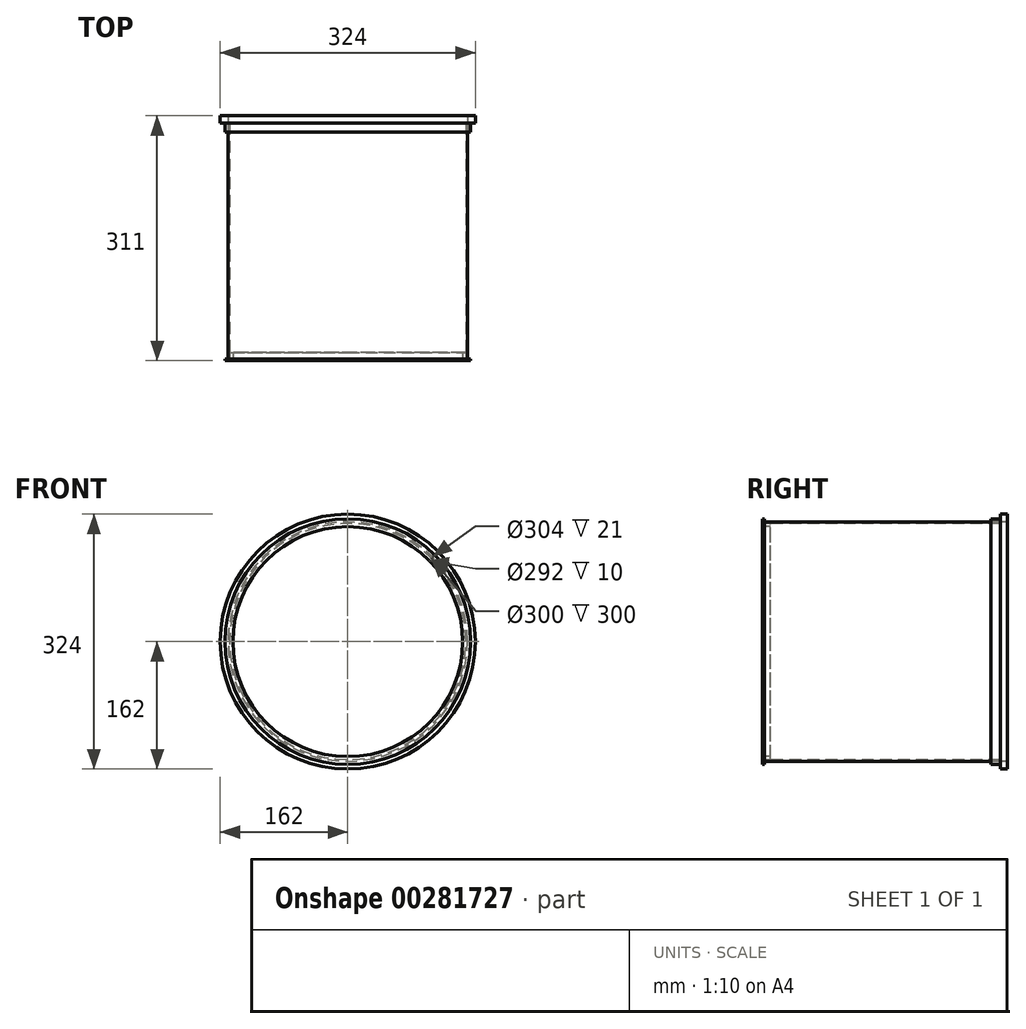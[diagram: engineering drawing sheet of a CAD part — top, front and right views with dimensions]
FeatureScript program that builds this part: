
annotation { "Feature Type Name" : "Feature", "Feature Type Description" : "" }
export const myFeature = defineFeature(function(context is Context, id is Id, definition is map)
    precondition{}
    {
        {
            assignVariable(context, id + "F0", {"name" : "DS_Length", "anyValue" : 300});
        }
        {
            var Q0;
            Q0=qCreatedBy(makeId("Front.planeOp"),FACE);
            var sketch = newSketch(context, id + "F1", { "sketchPlane" : qUnion([Q0])});
            skCircle(sketch, "E0", {"center": v(0, 0) * mm, "radius": 150 * mm});
            skCircle(sketch, "E1", {"center": v(0, 0) * mm, "radius": 152 * mm});
            skSolve(sketch);
        }
        {
            var Q0;
            Q0=makeQuery(id+"F1.imprint","IMPRINT",FACE,{"disambiguationData":[TD([[makeQuery(id+"F1.imprint","IMPRINT",EDGE,{"derivedFrom":sQuery(id+"F1.wireOp",EDGE,"E0")}),-1.0]])]});
            extrude(context, id + "F2", {"entities" : qUnion([Q0]), "oppositeDirection" : true, "depth" : (getVariable(context, 'DS_Length')) * mm, "offsetDistance" : 25 * mm});
        }
        {
            var Q0;
            Q0=qCreatedBy(makeId("Right.planeOp"),FACE);
            var sketch = newSketch(context, id + "F3", { "sketchPlane" : qUnion([Q0])});
            skLineSegment(sketch, "E2", {"start": v(309, 162) * mm, "end": v(309, 152) * mm});
            skLineSegment(sketch, "E3", {"start": v(309, 152) * mm, "end": v(288, 152) * mm});
            skLineSegment(sketch, "E4", {"start": v(288, 152) * mm, "end": v(288, 156) * mm});
            skLineSegment(sketch, "E5", {"start": v(288, 156) * mm, "end": v(300, 156) * mm});
            skLineSegment(sketch, "E6", {"start": v(300, 156) * mm, "end": v(300, 162) * mm});
            skLineSegment(sketch, "E7", {"start": v(300, 162) * mm, "end": v(309, 162) * mm});
            skLineSegment(sketch, "E8", {"start": v(-26.86, 0) * mm, "end": v(353.55, 0) * mm, "construction": true});
            skLineSegment(sketch, "E9", {"start": v(8, 150) * mm, "end": v(8, 146) * mm});
            skLineSegment(sketch, "E10", {"start": v(8, 146) * mm, "end": v(-2, 146) * mm});
            skLineSegment(sketch, "E11", {"start": v(-2, 146) * mm, "end": v(-2, 156) * mm});
            skLineSegment(sketch, "E12", {"start": v(-2, 156) * mm, "end": v(0, 156) * mm});
            skLineSegment(sketch, "E13", {"start": v(0, 156) * mm, "end": v(0, 150) * mm});
            skLineSegment(sketch, "E14", {"start": v(0, 150) * mm, "end": v(8, 150) * mm});
            skSolve(sketch);
        }
        {
            var Q0;
            Q0=makeQuery(id+"F3.imprint","IMPRINT",FACE,{"disambiguationData":[TD([[makeQuery(id+"F3.imprint","IMPRINT",EDGE,{"derivedFrom":sQuery(id+"F3.wireOp",EDGE,"E2")}),-1.0]])]});
            var Q1;
            Q1=sQuery(id+"F3.wireOp",EDGE,"E8");
            revolve(context, id + "F4", {"entities" : qUnion([Q0]), "axis" : qUnion([Q1]), "revolveType" : RevolveType.FULL});
        }
        {
            var Q0;
            Q0=makeQuery(id+"F3.imprint","IMPRINT",FACE,{"disambiguationData":[TD([[makeQuery(id+"F3.imprint","IMPRINT",EDGE,{"derivedFrom":sQuery(id+"F3.wireOp",EDGE,"E9")}),-1.0]])]});
            var Q1;
            Q1=sQuery(id+"F3.wireOp",EDGE,"E10");
            var Q2;
            Q2=sQuery(id+"F3.wireOp",EDGE,"E9");
            var Q3;
            Q3=sQuery(id+"F3.wireOp",EDGE,"E13");
            var Q4;
            Q4=sQuery(id+"F3.wireOp",EDGE,"E11");
            var Q5;
            Q5=sQuery(id+"F3.wireOp",EDGE,"E14");
            var Q6;
            Q6=sQuery(id+"F3.wireOp",EDGE,"E12");
            var Q7;
            Q7=sQuery(id+"F3.wireOp",EDGE,"E8");
            revolve(context, id + "F5", {"entities" : qUnion([Q0]), "surfaceEntities" : qUnion([Q1, Q2, Q3, Q4, Q5, Q6]), "axis" : qUnion([Q7]), "revolveType" : RevolveType.FULL});
        }
    });
